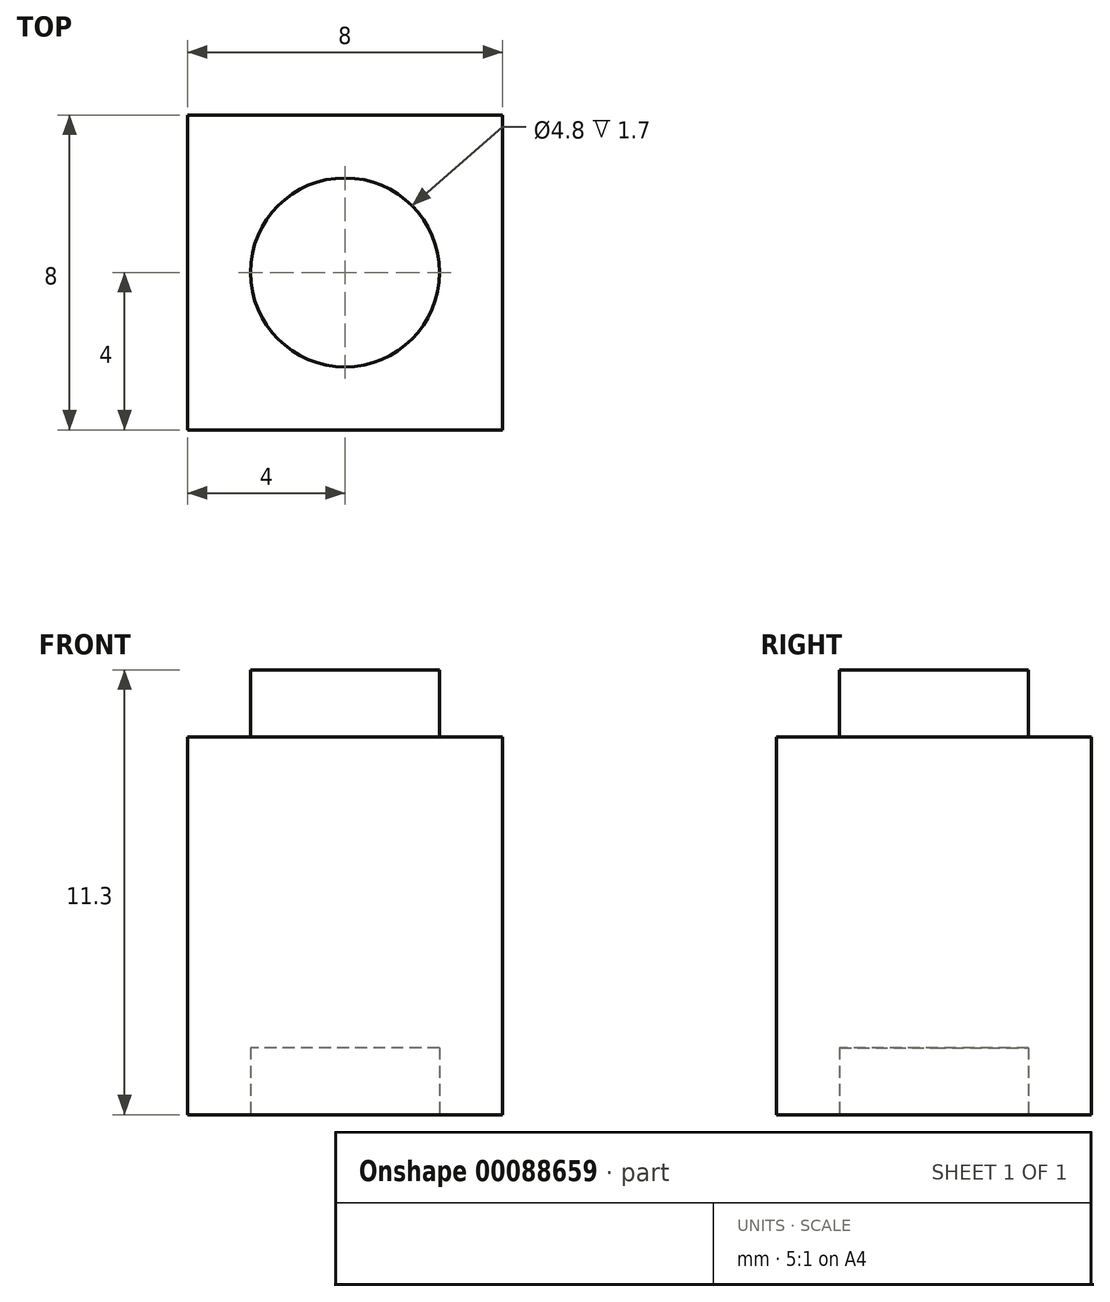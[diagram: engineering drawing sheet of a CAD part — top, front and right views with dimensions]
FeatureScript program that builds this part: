
annotation { "Feature Type Name" : "Feature", "Feature Type Description" : "" }
export const myFeature = defineFeature(function(context is Context, id is Id, definition is map)
    precondition{}
    {
        {
            var Q0;
            Q0=qCreatedBy(makeId("Front.planeOp"),FACE);
            var sketch = newSketch(context, id + "F0", { "sketchPlane" : qUnion([Q0])});
            skLineSegment(sketch, "E0.bottom", {"start": v(-4, 9.6) * mm, "end": v(-2.4, 9.6) * mm});
            skLineSegment(sketch, "E0.top", {"start": v(-4, 0) * mm, "end": v(4, 0) * mm});
            skLineSegment(sketch, "E0.left", {"start": v(-4, 9.6) * mm, "end": v(-4, 0) * mm});
            skLineSegment(sketch, "E0.right", {"start": v(4, 9.6) * mm, "end": v(4, 0) * mm});
            skLineSegment(sketch, "E1.top", {"start": v(-2.4, 11.3) * mm, "end": v(2.4, 11.3) * mm});
            skLineSegment(sketch, "E1.left", {"start": v(-2.4, 9.6) * mm, "end": v(-2.4, 11.3) * mm});
            skLineSegment(sketch, "E1.right", {"start": v(2.4, 9.6) * mm, "end": v(2.4, 11.3) * mm});
            skLineSegment(sketch, "E2", {"start": v(0, 0) * mm, "end": v(0, 24.04) * mm, "construction": true});
            skLineSegment(sketch, "E3.trimOffspring", {"start": v(2.4, 9.6) * mm, "end": v(4, 9.6) * mm});
            skSolve(sketch);
        }
        {
            var Q0;
            Q0=makeQuery(id+"F0.imprint","IMPRINT",FACE,{"disambiguationData":[TD([[makeQuery(id+"F0.imprint","IMPRINT",EDGE,{"derivedFrom":sQuery(id+"F0.wireOp",EDGE,"E0.bottom")}),-1.0]])]});
            extrude(context, id + "F1", {"entities" : qUnion([Q0]), "depth" : 8 * mm});
        }
        {
            var Q0;
            Q0=qCreatedBy(makeId("Top.planeOp"),FACE);
            var Q1;
            Q1=makeQuery(id+"F1.opExtrude","CAP_VERTEX",VERTEX,{"disambiguationData":[OSD([sQuery(id+"F0.wireOp",EDGE,"E1.top"),sQuery(id+"F0.wireOp",EDGE,"E1.right")])],"isStart":true});
            cPlane(context, id + "F2", {"entities" : qUnion([Q0, Q1]), "cplaneType" : CPlaneType.PLANE_POINT, "offset" : 152.4 * mm, "width" : 152.4 * mm, "height" : 152.4 * mm});
        }
        {
            var Q0;
            Q0=qCreatedBy(id+"F2.planeOp",FACE);
            var sketch = newSketch(context, id + "F3", { "sketchPlane" : qUnion([Q0])});
            skLineSegment(sketch, "E4.0", {"start": v(-4, -8) * mm, "end": v(-4, 0) * mm});
            skLineSegment(sketch, "E5.0", {"start": v(4, -8) * mm, "end": v(4, 0) * mm});
            skLineSegment(sketch, "E6", {"start": v(-4, 0) * mm, "end": v(4, 0) * mm});
            skLineSegment(sketch, "E7", {"start": v(-4, -8) * mm, "end": v(4, -8) * mm});
            skLineSegment(sketch, "E8", {"start": v(-4, 0) * mm, "end": v(4, -8) * mm, "construction": true});
            skLineSegment(sketch, "E9", {"start": v(-4, -8) * mm, "end": v(4, 0) * mm, "construction": true});
            skCircle(sketch, "E10", {"center": v(0, -4) * mm, "radius": 2.4 * mm});
            skSolve(sketch);
        }
        {
            var Q0;
            Q0 = qSketchRegion(id + "F3", true);
            var Q1;
            Q1=makeQuery(id+"F1.opExtrude","SWEPT_FACE",FACE,{"disambiguationData":[OSD([sQuery(id+"F0.wireOp",EDGE,"E0.bottom")])]});
            extrude(context, id + "F4", {"entities" : qUnion([Q0]), "operationType" : NewBodyOperationType.REMOVE, "endBound" : BoundingType.UP_TO_SURFACE, "oppositeDirection" : true, "endBoundEntityFace" : qUnion([Q1]), "depth" : 25.4 * mm});
        }
        {
            var Q0;
            Q0=qCreatedBy(makeId("Top.planeOp"),FACE);
            var sketch = newSketch(context, id + "F5", { "sketchPlane" : qUnion([Q0])});
            skCircle(sketch, "E11.0", {"center": v(0, -4) * mm, "radius": 2.4 * mm});
            skSolve(sketch);
        }
        {
            var Q0;
            Q0=makeQuery(id+"F5.imprint","IMPRINT",FACE,{"disambiguationData":[TD([[makeQuery(id+"F5.imprint","IMPRINT",EDGE,{"derivedFrom":sQuery(id+"F5.wireOp",EDGE,"E11.0")}),1.0]])]});
            extrude(context, id + "F6", {"entities" : qUnion([Q0]), "operationType" : NewBodyOperationType.REMOVE, "depth" : 1.7 * mm});
        }
    });
